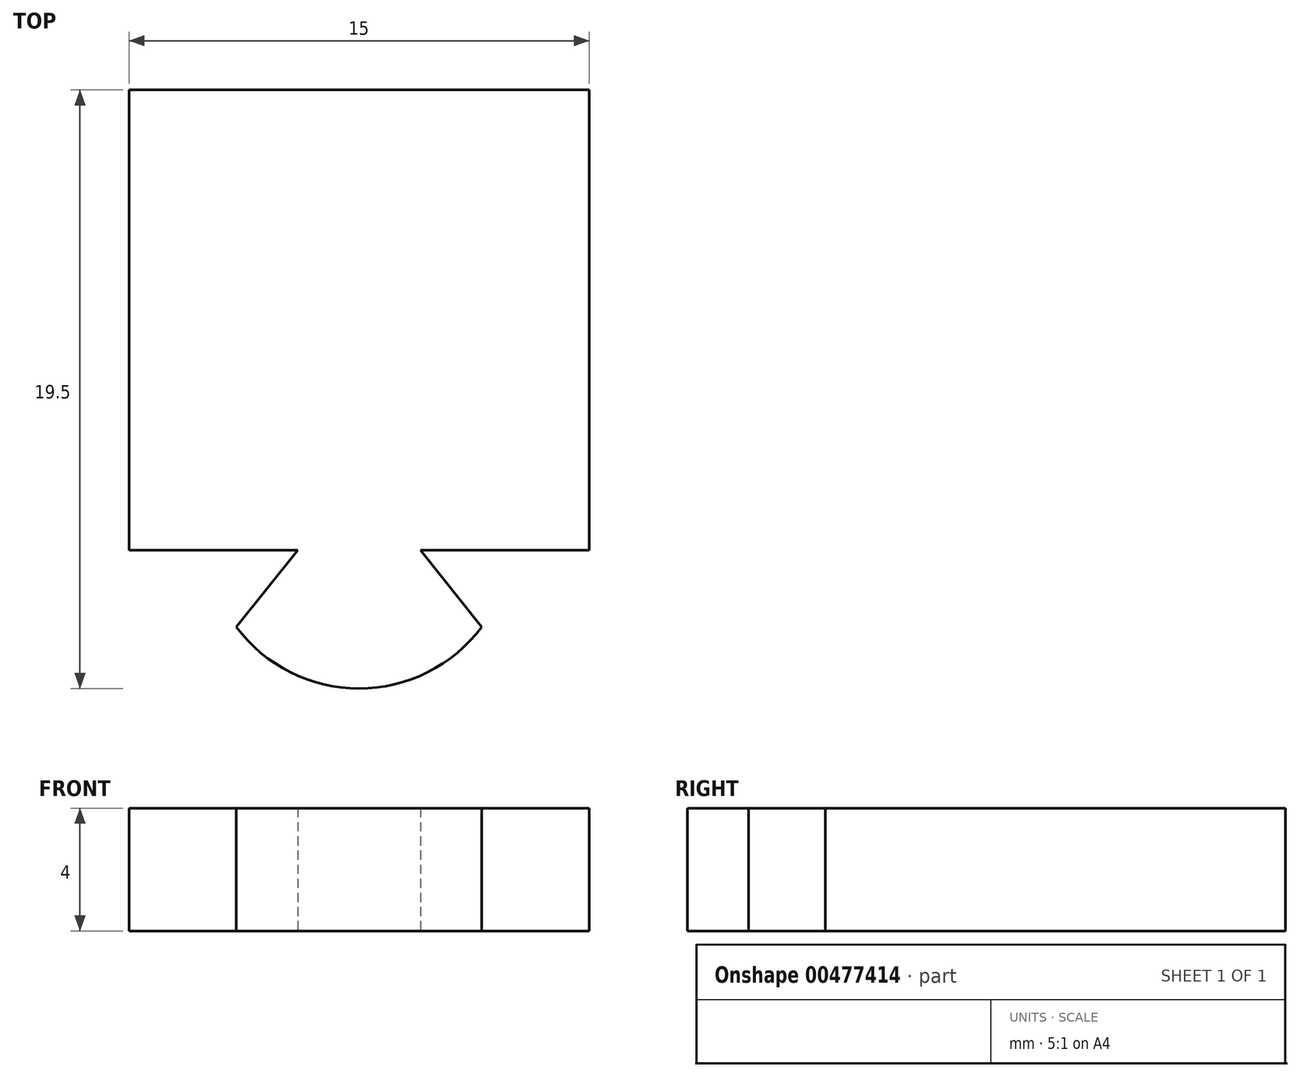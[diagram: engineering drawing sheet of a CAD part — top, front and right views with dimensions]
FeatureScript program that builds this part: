
annotation { "Feature Type Name" : "Feature", "Feature Type Description" : "" }
export const myFeature = defineFeature(function(context is Context, id is Id, definition is map)
    precondition{}
    {
        {
            var Q0;
            Q0=qCreatedBy(makeId("Top.planeOp"),FACE);
            var sketch = newSketch(context, id + "F0", { "sketchPlane" : qUnion([Q0])});
            skLineSegment(sketch, "E0.bottom", {"start": v(7.5, 7.5) * mm, "end": v(-7.5, 7.5) * mm});
            skLineSegment(sketch, "E0.top", {"start": v(7.5, -7.5) * mm, "end": v(-7.5, -7.5) * mm});
            skLineSegment(sketch, "E0.left", {"start": v(7.5, 7.5) * mm, "end": v(7.5, -7.5) * mm});
            skLineSegment(sketch, "E0.right", {"start": v(-7.5, 7.5) * mm, "end": v(-7.5, -7.5) * mm});
            skPoint(sketch, "E0.middle", {"position": v(0, 0) * mm});
            skLineSegment(sketch, "E1", {"start": v(0, 12.48) * mm, "end": v(0, -18.86) * mm, "construction": true});
            skPoint(sketch, "E1.endSnap0", {"position": v(0, -7.5) * mm});
            skLineSegment(sketch, "E2", {"start": v(-2, -7.5) * mm, "end": v(-4, -10) * mm});
            skLineSegment(sketch, "E3", {"start": v(2, -7.5) * mm, "end": v(4, -10) * mm});
            skArc(sketch, "E4", {"start": v(-4, -10) * mm, "mid": v(0, -12) * mm, "end": v(4, -10) * mm});
            skSolve(sketch);
        }
        {
            var Q0;
            Q0 = qSketchRegion(id + "F0", true);
            extrude(context, id + "F1", {"entities" : qUnion([Q0]), "depth" : 4 * mm, "offsetDistance" : 25 * mm});
        }
    });
